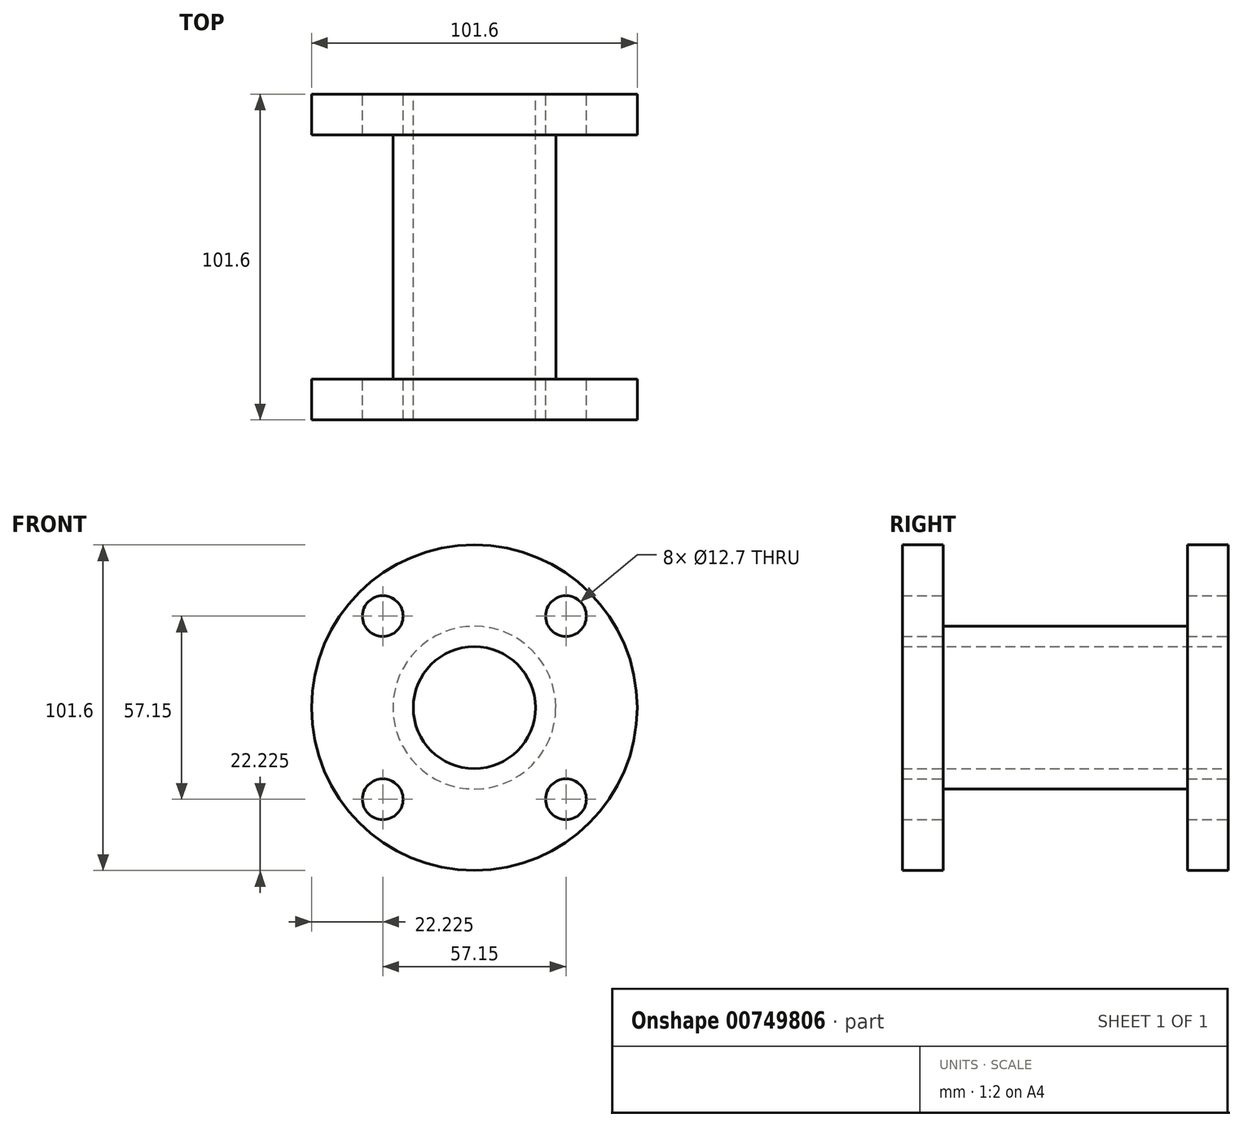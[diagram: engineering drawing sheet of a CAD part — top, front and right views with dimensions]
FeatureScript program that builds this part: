
annotation { "Feature Type Name" : "Feature", "Feature Type Description" : "" }
export const myFeature = defineFeature(function(context is Context, id is Id, definition is map)
    precondition{}
    {
        {
            var Q0;
            Q0=qCreatedBy(makeId("Front.planeOp"),FACE);
            var sketch = newSketch(context, id + "F0", { "sketchPlane" : qUnion([Q0])});
            skCircle(sketch, "E0", {"center": v(0, 0) * mm, "radius": 19.05 * mm});
            skCircle(sketch, "E1", {"center": v(0, 0) * mm, "radius": 25.4 * mm});
            skCircle(sketch, "E2", {"center": v(0, 0) * mm, "radius": 50.8 * mm});
            skCircle(sketch, "E3", {"center": v(-28.58, 28.58) * mm, "radius": 6.35 * mm});
            skCircle(sketch, "E4", {"center": v(28.58, 28.58) * mm, "radius": 6.35 * mm});
            skCircle(sketch, "E5", {"center": v(28.58, -28.58) * mm, "radius": 6.35 * mm});
            skCircle(sketch, "E6", {"center": v(-28.58, -28.58) * mm, "radius": 6.35 * mm});
            skSolve(sketch);
        }
        {
            var Q0;
            Q0=makeQuery(id+"F0.imprint","IMPRINT",FACE,{"disambiguationData":[TD([[makeQuery(id+"F0.imprint","IMPRINT",EDGE,{"derivedFrom":sQuery(id+"F0.wireOp",EDGE,"E1")}),-1.0]])]});
            var Q1;
            Q1=makeQuery(id+"F0.imprint","IMPRINT",FACE,{"disambiguationData":[TD([[makeQuery(id+"F0.imprint","IMPRINT",EDGE,{"derivedFrom":sQuery(id+"F0.wireOp",EDGE,"E0")}),-1.0]])]});
            extrude(context, id + "F1", {"entities" : qUnion([Q0, Q1]), "depth" : 12.7 * mm, "offsetDistance" : 25.4 * mm});
        }
        {
            var Q0;
            Q0=makeQuery(id+"F1.opExtrude","CAP_FACE",FACE,{"disambiguationData":[OSD([sQuery(id+"F0.wireOp",EDGE,"E0"),sQuery(id+"F0.wireOp",EDGE,"E2"),sQuery(id+"F0.wireOp",EDGE,"E3"),sQuery(id+"F0.wireOp",EDGE,"E4"),sQuery(id+"F0.wireOp",EDGE,"E5"),sQuery(id+"F0.wireOp",EDGE,"E6")])],"isStart":false});
            var sketch = newSketch(context, id + "F2", { "sketchPlane" : qUnion([Q0])});
            skCircle(sketch, "E7", {"center": v(0, 0) * mm, "radius": 25.4 * mm});
            skSolve(sketch);
        }
        {
            var Q0;
            Q0=makeQuery(id+"F2.imprint","IMPRINT",FACE,{"disambiguationData":[TD([[makeQuery(id+"F2.imprint","IMPRINT",EDGE,{"derivedFrom":sQuery(id+"F2.wireOp",EDGE,"E7")}),1.0]])]});
            extrude(context, id + "F3", {"entities" : qUnion([Q0]), "operationType" : NewBodyOperationType.ADD, "depth" : 76.2 * mm, "offsetDistance" : 25.4 * mm});
        }
        {
            var Q0;
            Q0=makeQuery(id+"F3.opExtrude","CAP_FACE",FACE,{"disambiguationData":[OSD([sQuery(id+"F0.wireOp",EDGE,"E0"),sQuery(id+"F2.wireOp",EDGE,"E7")])],"isStart":false});
            var sketch = newSketch(context, id + "F4", { "sketchPlane" : qUnion([Q0])});
            skCircle(sketch, "E8", {"center": v(0, 0) * mm, "radius": 50.8 * mm});
            skCircle(sketch, "E9", {"center": v(-28.58, 28.58) * mm, "radius": 6.35 * mm});
            skCircle(sketch, "E10", {"center": v(28.58, 28.58) * mm, "radius": 6.35 * mm});
            skCircle(sketch, "E11", {"center": v(28.58, -28.58) * mm, "radius": 6.35 * mm});
            skCircle(sketch, "E12", {"center": v(-28.58, -28.58) * mm, "radius": 6.35 * mm});
            skSolve(sketch);
        }
        {
            var Q0;
            Q0=makeQuery(id+"F4.imprint","IMPRINT",FACE,{"disambiguationData":[TD([[makeQuery(id+"F4.imprint","IMPRINT",EDGE,{"derivedFrom":sQuery(id+"F4.wireOp",EDGE,"E8")}),1.0]])]});
            var Q1;
            Q1=makeQuery(id+"F4.imprint","IMPRINT",FACE,{"disambiguationData":[TD([[makeQuery(id+"F4.imprint","IMPRINT",EDGE,{"derivedFrom":makeQuery(id+"F3.opExtrude","CAP_EDGE",EDGE,{"disambiguationData":[OSD([sQuery(id+"F2.wireOp",EDGE,"E7")])],"isStart":false})}),1.0]])]});
            extrude(context, id + "F5", {"entities" : qUnion([Q0, Q1]), "operationType" : NewBodyOperationType.ADD, "depth" : 12.7 * mm, "offsetDistance" : 25.4 * mm});
        }
    });
